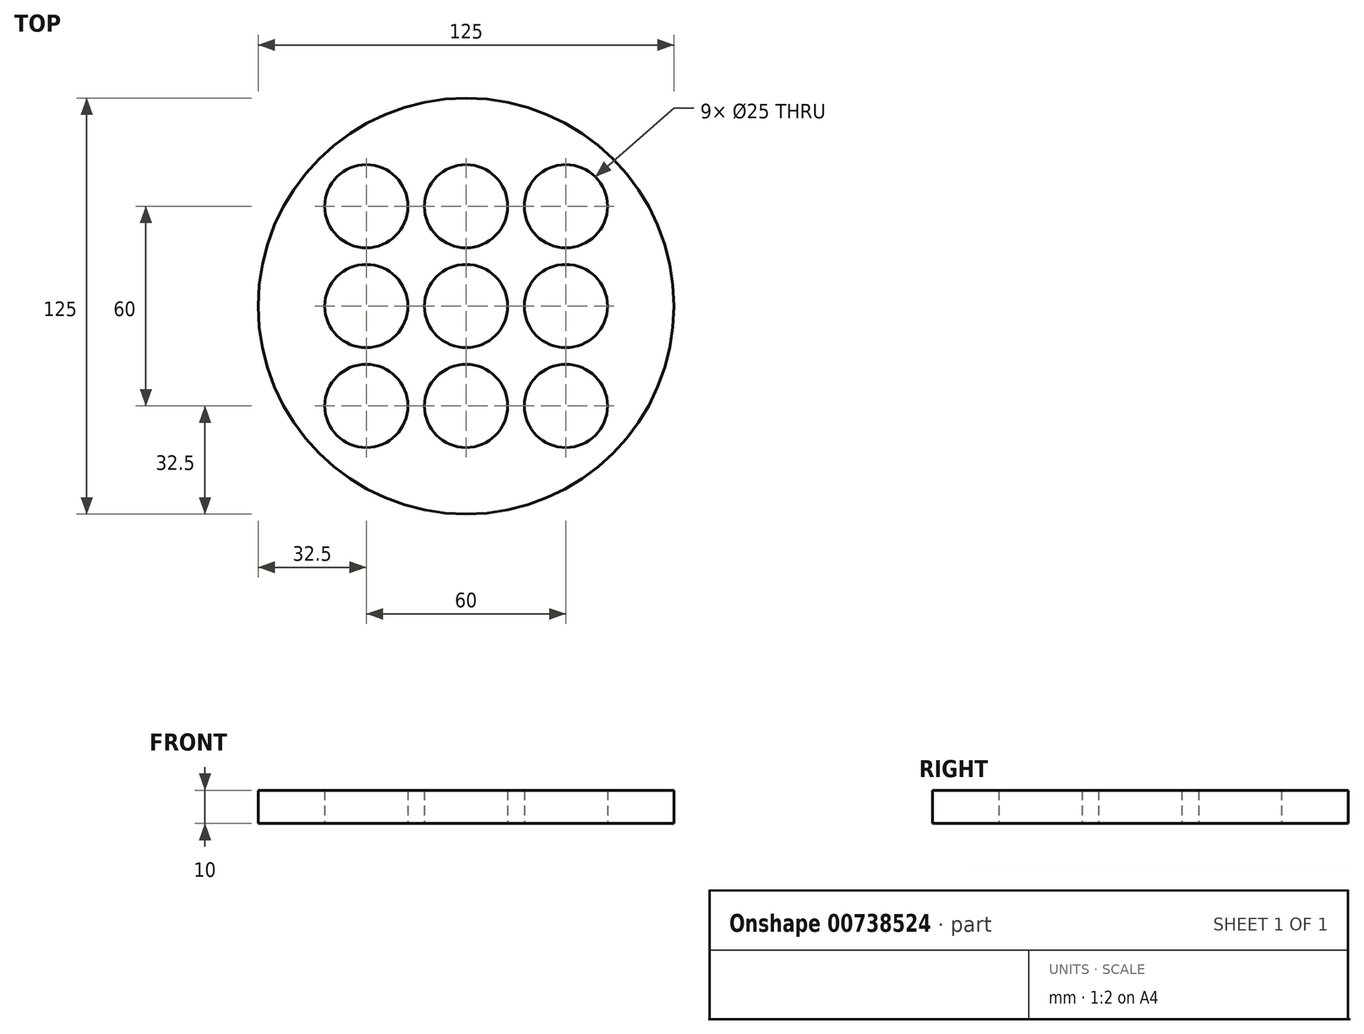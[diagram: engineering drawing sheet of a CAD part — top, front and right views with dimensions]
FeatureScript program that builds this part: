
annotation { "Feature Type Name" : "Feature", "Feature Type Description" : "" }
export const myFeature = defineFeature(function(context is Context, id is Id, definition is map)
    precondition{}
    {
        {
            var Q0;
            Q0=qCreatedBy(makeId("Top.planeOp"),FACE);
            var sketch = newSketch(context, id + "F0", { "sketchPlane" : qUnion([Q0])});
            skCircle(sketch, "E0", {"center": v(0, 0) * mm, "radius": 12.5 * mm});
            skCircle(sketch, "E1", {"center": v(0, -30) * mm, "radius": 12.5 * mm});
            skCircle(sketch, "E2", {"center": v(-30, -30) * mm, "radius": 12.5 * mm});
            skCircle(sketch, "E3", {"center": v(-30, 0) * mm, "radius": 12.5 * mm});
            skCircle(sketch, "E4", {"center": v(-30, 30) * mm, "radius": 12.5 * mm});
            skCircle(sketch, "E5", {"center": v(0, 30) * mm, "radius": 12.5 * mm});
            skCircle(sketch, "E6", {"center": v(30, 30) * mm, "radius": 12.5 * mm});
            skCircle(sketch, "E7", {"center": v(30, 0) * mm, "radius": 12.5 * mm});
            skCircle(sketch, "E8", {"center": v(30, -30) * mm, "radius": 12.5 * mm});
            skPoint(sketch, "E9.orphan", {"position": v(-62.5, 30) * mm});
            skPoint(sketch, "E10.orphan", {"position": v(0, -62.5) * mm});
            skPoint(sketch, "E11.orphan", {"position": v(-62.5, -30) * mm});
            skPoint(sketch, "E12.orphan", {"position": v(62.5, 62.5) * mm});
            skPoint(sketch, "E13.orphan", {"position": v(62.5, -62.5) * mm});
            skPoint(sketch, "E14.end.orphan", {"position": v(-62.5, -62.5) * mm});
            skPoint(sketch, "E15.0.start.orphan", {"position": v(62.5, 30) * mm});
            skPoint(sketch, "E16.orphan", {"position": v(62.5, 0) * mm});
            skPoint(sketch, "E17.0.start.orphan", {"position": v(62.5, -30) * mm});
            skCircle(sketch, "E18", {"center": v(0, 0) * mm, "radius": 62.5 * mm});
            skSolve(sketch);
        }
        {
            var Q0;
            Q0=qSketchRegion(id+"F0",true);
            extrude(context, id + "F1", {"entities" : qUnion([Q0]), "depth" : 10 * mm, "offsetDistance" : 25 * mm});
        }
    });
